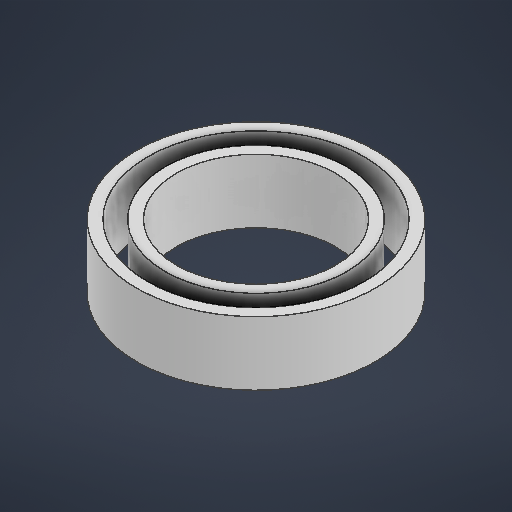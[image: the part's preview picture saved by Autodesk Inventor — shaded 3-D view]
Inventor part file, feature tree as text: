
AUTODESK INVENTOR PART (.ipt)
format: ipt  version: 2025 (Build 290162010, 162A)  size: 215,040 bytes
history: native  units: mm
features: extrude x2, sketch x2
ambient origin geometry x8: Origin, YZ Plane, XZ Plane, XY Plane, X Axis, Y Axis, Z Axis, Center Point
bodies: Solid1 (feature_tree)
feature tree (4):
  extrude  "Extrusion1"  Depth=10.0mm
  extrude  "Extrusion2"  Depth=4.0mm
  sketch  "Sketch1"  dims[d0=10.0mm d1=15.0mm]
  sketch  "Sketch2"  dims[d2=4.0mm d3=0.0mm d4=0.7mm d5=0.7mm d6=4.0mm d7=0.0mm]
